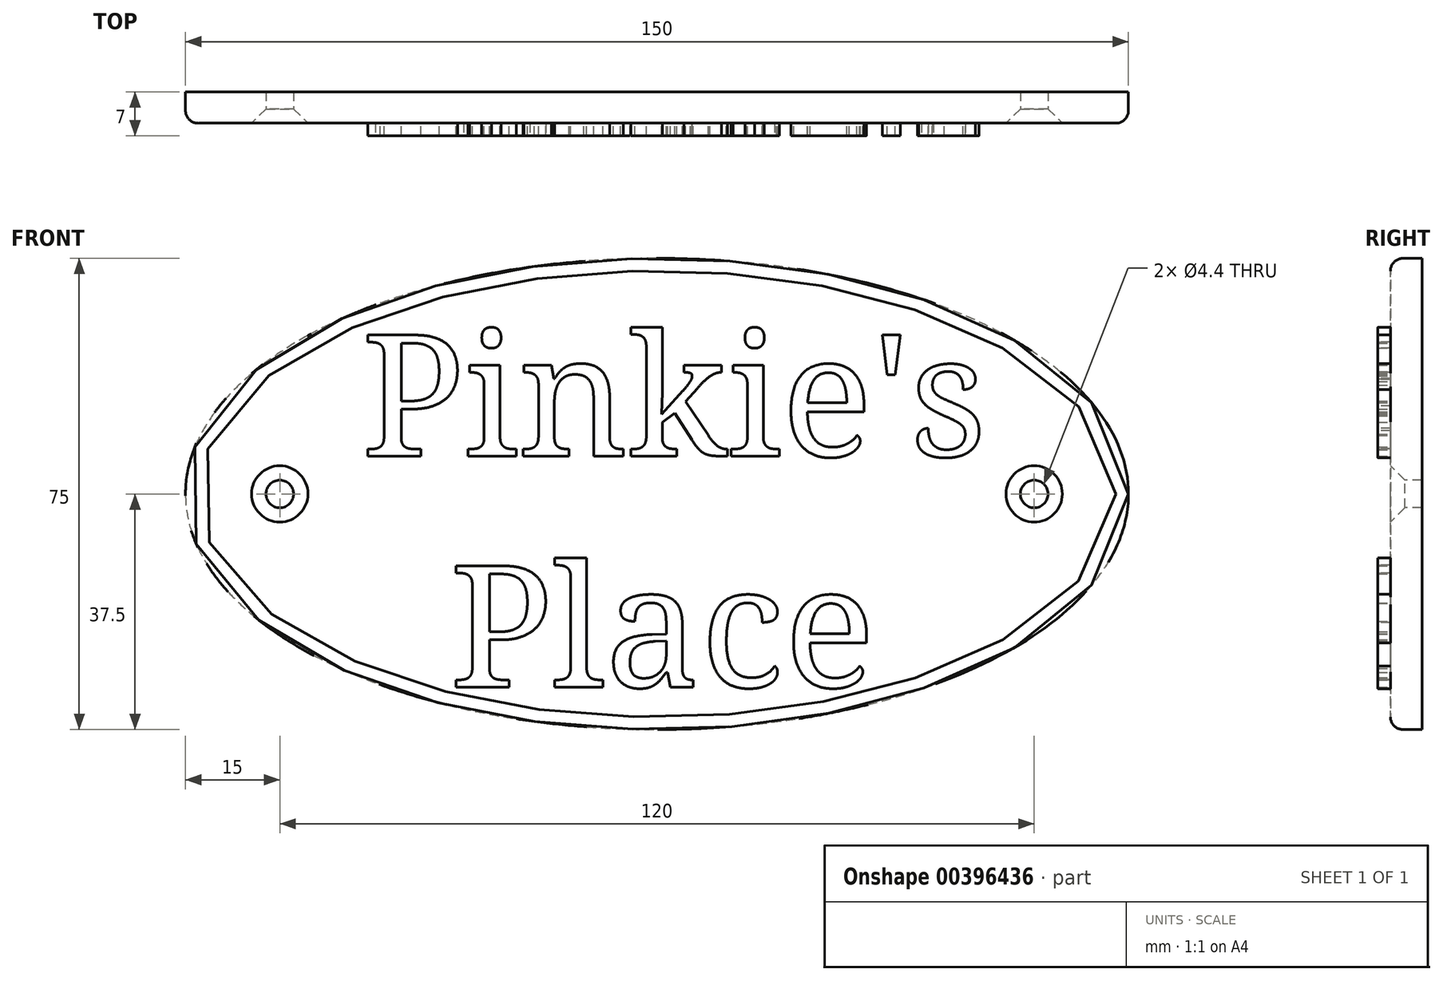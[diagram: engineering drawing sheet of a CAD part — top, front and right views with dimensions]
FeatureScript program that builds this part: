
annotation { "Feature Type Name" : "Feature", "Feature Type Description" : "" }
export const myFeature = defineFeature(function(context is Context, id is Id, definition is map)
    precondition{}
    {
        {
            var Q0;
            Q0=qCreatedBy(makeId("Front.planeOp"),FACE);
            var sketch = newSketch(context, id + "F0", { "sketchPlane" : qUnion([Q0])});
            skEllipse(sketch, "E0", {"center": v(0, 0) * mm, "majorRadius": 75 * mm, "minorRadius": 37.5 * mm, "majorAxis": v(1, 0)});
            skSolve(sketch);
        }
        {
            var Q0;
            Q0=qSketchRegion(id+"F0",true);
            extrude(context, id + "F1", {"entities" : qUnion([Q0]), "oppositeDirection" : true, "depth" : 5 * mm});
        }
        {
            var Q0;
            Q0=makeQuery(id+"F1.opExtrude","CAP_FACE",FACE,{"disambiguationData":[OSD([sQuery(id+"F0.wireOp",EDGE,"E0")])],"isStart":true});
            var sketch = newSketch(context, id + "F2", { "sketchPlane" : qUnion([Q0])});
            skText(sketch, "E1", { "text": "Pinkie\'s\n  Place", "fontName": "NotoSerif-Regular.ttf"});
            const initialGuessF2  = {"E1": [-0.047, 0.006, 1, 0, 0.01945]};
            skSetInitialGuess(sketch, initialGuessF2);
            skSolve(sketch);
        }
        {
            var Q0;
            Q0=qSketchRegion(id+"F2",true);
            extrude(context, id + "F3", {"entities" : qUnion([Q0]), "operationType" : NewBodyOperationType.ADD, "depth" : 2 * mm});
        }
        {
            var Q0;
            {var subQ0=sQuery(id+"F0.wireOp",EDGE,"E0");Q0=makeQuery(id+"F3.boolean.opBoolean","SPLIT",FACE,{"disambiguationData":[TD([makeQuery(id+"F1.opExtrude","SWEPT_FACE",FACE,{"disambiguationData":[OSD([subQ0])]})])],"derivedFrom":makeQuery(id+"F1.opExtrude","CAP_FACE",FACE,{"disambiguationData":[OSD([subQ0])],"isStart":true})});}
            var sketch = newSketch(context, id + "F4", { "sketchPlane" : qUnion([Q0])});
            skPoint(sketch, "E2", {"position": v(0, 0) * mm});
            skPoint(sketch, "E3", {"position": v(-60, 0) * mm});
            skPoint(sketch, "E4.MirrorP", {"position": v(60, 0) * mm});
            skSolve(sketch);
        }
        {
            var Q0;
            Q0=sQuery(id+"F4.wireOp",VERTEX,"E3");
            var Q1;
            Q1=sQuery(id+"F4.wireOp",VERTEX,"E4.MirrorP");
            var Q2;
            Q2=makeQuery(id+"F1.opExtrude","SWEPT_BODY",BODY,{"disambiguationData":[OSD([sQuery(id+"F0.wireOp",EDGE,"E0")])]});
            hole(context, id + "F5", {"style" : HoleStyle.C_SINK, "endStyle" : HoleEndStyle.THROUGH, "standardTappedOrClearance" : lookupTablePath({ "standard" : "ISO", "fit" : "Normal", "size" : "M4", "type" : "Clearance" }), "standardBlindInLast" : lookupTablePath({ "fit" : "Standard", "standard" : "ISO", "size" : "M4", "type" : "Clearance" }), "holeDiameter" : 4.4 * mm, "cSinkDiameter" : 8.96 * mm, "cSinkAngle" : 90 * degree, "isTappedThrough" : true, "tappedDepth" : 12 * mm, "tapClearance" : 3, "locations" : qUnion([Q0, Q1]), "scope" : qUnion([Q2])});
        }
        {
            var Q0;
            Q0=makeQuery(id+"F1.opExtrude","CAP_EDGE",EDGE,{"disambiguationData":[OSD([sQuery(id+"F0.wireOp",EDGE,"E0")])],"isStart":true});
            fillet(context, id + "F6", {"entities" : qUnion([Q0]), "radius" : 2 * mm, "tangentPropagation" : true, "allowEdgeOverflow" : false});
        }
    });
